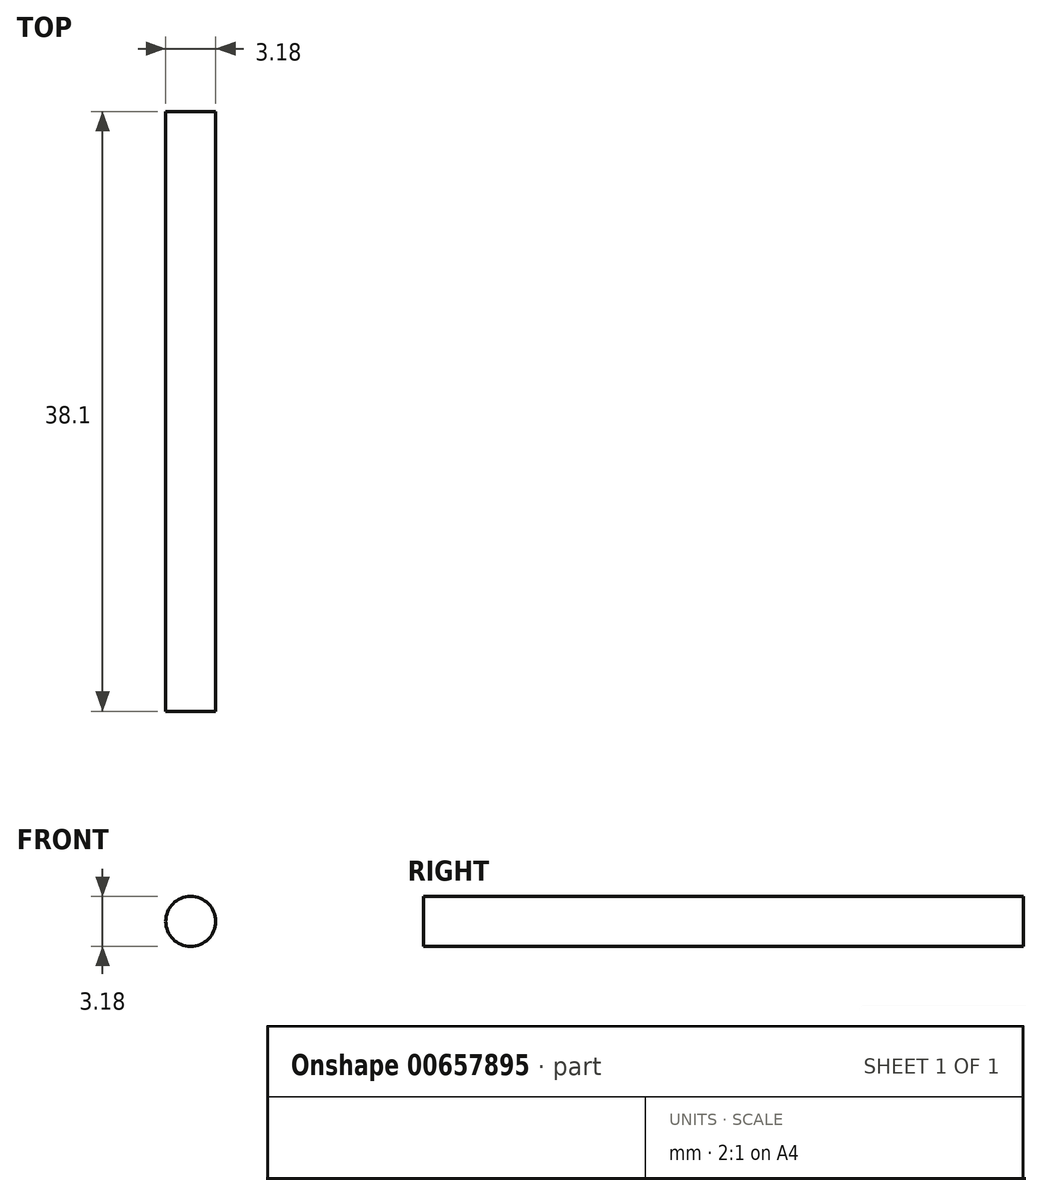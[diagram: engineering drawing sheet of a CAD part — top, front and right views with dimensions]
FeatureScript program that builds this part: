
annotation { "Feature Type Name" : "Feature", "Feature Type Description" : "" }
export const myFeature = defineFeature(function(context is Context, id is Id, definition is map)
    precondition{}
    {
        {
            var Q0;
            Q0=qCreatedBy(makeId("Front.planeOp"),FACE);
            var sketch = newSketch(context, id + "F0", { "sketchPlane" : qUnion([Q0])});
            skCircle(sketch, "E0", {"center": v(0, 0) * mm, "radius": 1.59 * mm});
            skSolve(sketch);
        }
        {
            var Q0;
            Q0 = qSketchRegion(id + "F0", true);
            extrude(context, id + "F1", {"entities" : qUnion([Q0]), "endBound" : BoundingType.SYMMETRIC, "depth" : 38.1 * mm, "offsetDistance" : 25.4 * mm});
        }
    });
